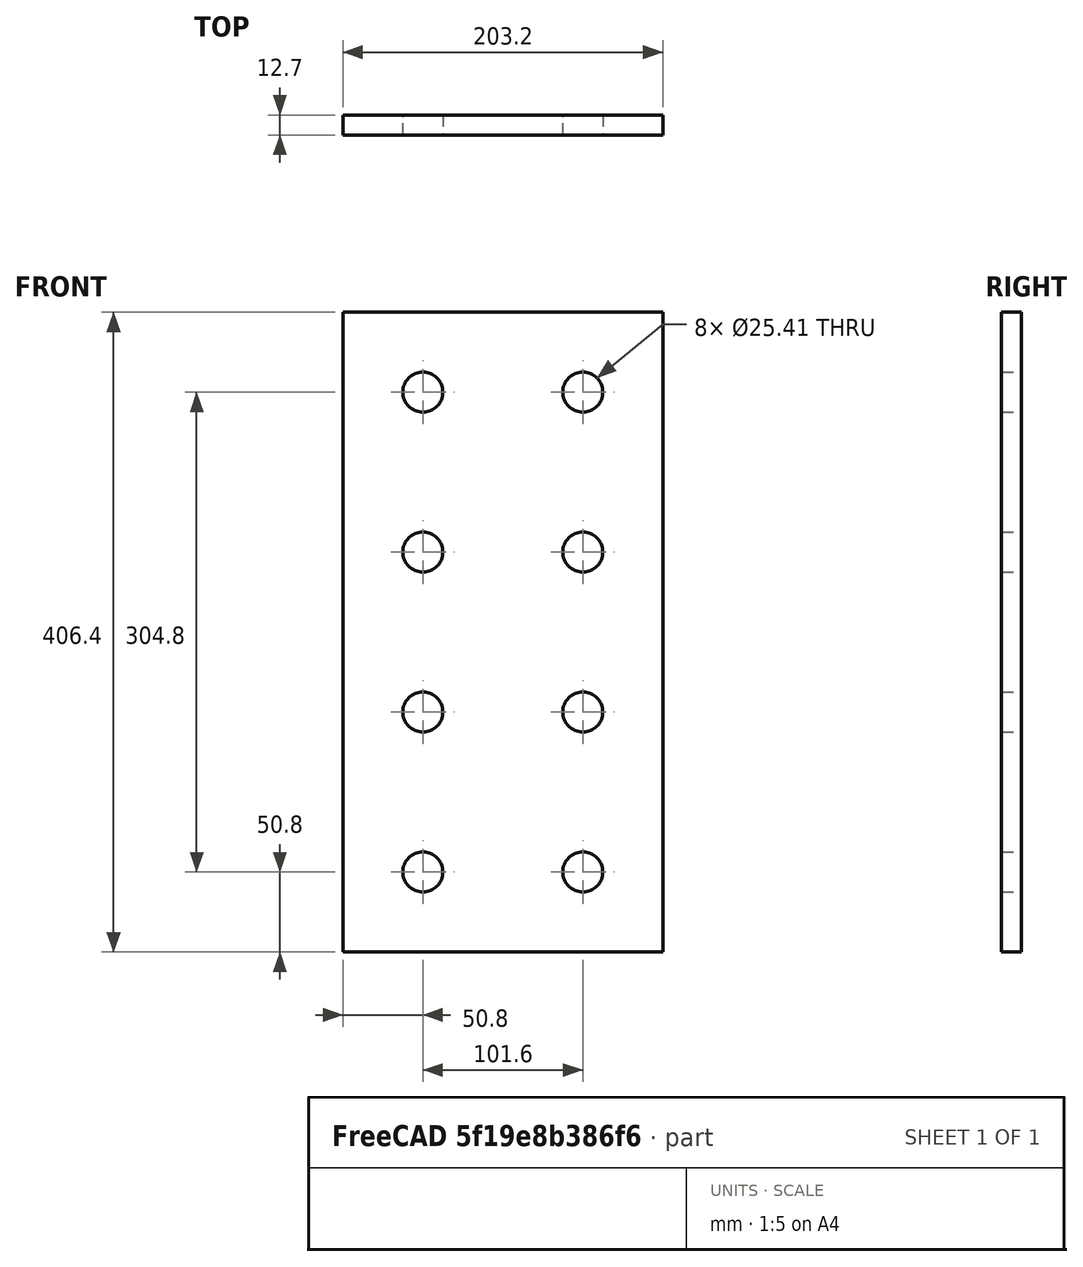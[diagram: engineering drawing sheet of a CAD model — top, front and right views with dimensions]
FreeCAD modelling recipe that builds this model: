
FCSTD DOCUMENT  (FreeCAD 0.16R6668 (Git))
Label: stock bonding plate
License: All rights reserved
LicenseURL: http://en.wikipedia.org/wiki/All_rights_reserved
objects: Sketcher::SketchObject×1, PartDesign::Pad×1
note: 3 computed .brp shape members not serialized (recipe doc carries the construction recipe); baked Part::Feature solids carry a one-line shape summary decoded from their .brp

FEATURE [Sketcher::SketchObject] Sketch
  Placement = pos=(0,0,0) rot=(1,0,0;1.5708rad)
  sketch-geometry (12):
    g0: LineSegment StartX=-101.6 StartY=203.2 StartZ=0 EndX=101.6 EndY=203.2 EndZ=0
    g1: LineSegment StartX=101.6 StartY=203.2 StartZ=0 EndX=101.6 EndY=-203.2 EndZ=0
    g2: LineSegment StartX=101.6 StartY=-203.2 StartZ=0 EndX=-101.6 EndY=-203.2 EndZ=0
    g3: LineSegment StartX=-101.6 StartY=-203.2 StartZ=0 EndX=-101.6 EndY=203.2 EndZ=0
    g4: Circle CenterX=-50.8 CenterY=-152.4 CenterZ=0 NormalX=0 NormalY=0 NormalZ=1 Radius=12.7046
    g5: Circle CenterX=-50.8 CenterY=-50.8 CenterZ=0 NormalX=0 NormalY=0 NormalZ=1 Radius=12.7046
    g6: Circle CenterX=50.8 CenterY=-50.8 CenterZ=0 NormalX=0 NormalY=0 NormalZ=1 Radius=12.7046
    g7: Circle CenterX=-50.8 CenterY=50.8 CenterZ=0 NormalX=0 NormalY=0 NormalZ=1 Radius=12.7046
    g8: Circle CenterX=50.8 CenterY=50.8 CenterZ=0 NormalX=0 NormalY=0 NormalZ=1 Radius=12.7046
    g9: Circle CenterX=-50.8 CenterY=152.4 CenterZ=0 NormalX=0 NormalY=0 NormalZ=1 Radius=12.7046
    g10: Circle CenterX=50.8 CenterY=152.4 CenterZ=0 NormalX=0 NormalY=0 NormalZ=1 Radius=12.7046
    g11: Circle CenterX=50.8 CenterY=-152.4 CenterZ=0 NormalX=0 NormalY=0 NormalZ=1 Radius=12.7046
  constraints (18):
    c: Coincident(g0,g1)
    c: Coincident(g1,g2)
    c: Coincident(g2,g3)
    c: Coincident(g3,g0)
    c: Horizontal(g0)
    c: Horizontal(g2)
    c: Vertical(g1)
    c: Vertical(g3)
    c: DistanceX(g0,g0) = 203.2
    c: DistanceY(g1,g1) = 406.4
    c: Radius(g11) = 12.7046
    c: Equal(g11,g4)
    c: Equal(g4,g6)
    c: Equal(g6,g5)
    c: Equal(g5,g8)
    c: Equal(g8,g7)
    c: Equal(g7,g10)
    c: Equal(g10,g9)
FEATURE [PartDesign::Pad] Pad
  Length = 12.7
  Length2 = 100
  Placement = pos=(0,0,0) rot=(1,0,0;1.5708rad)
  Sketch = -> Sketch
  Type = 0
